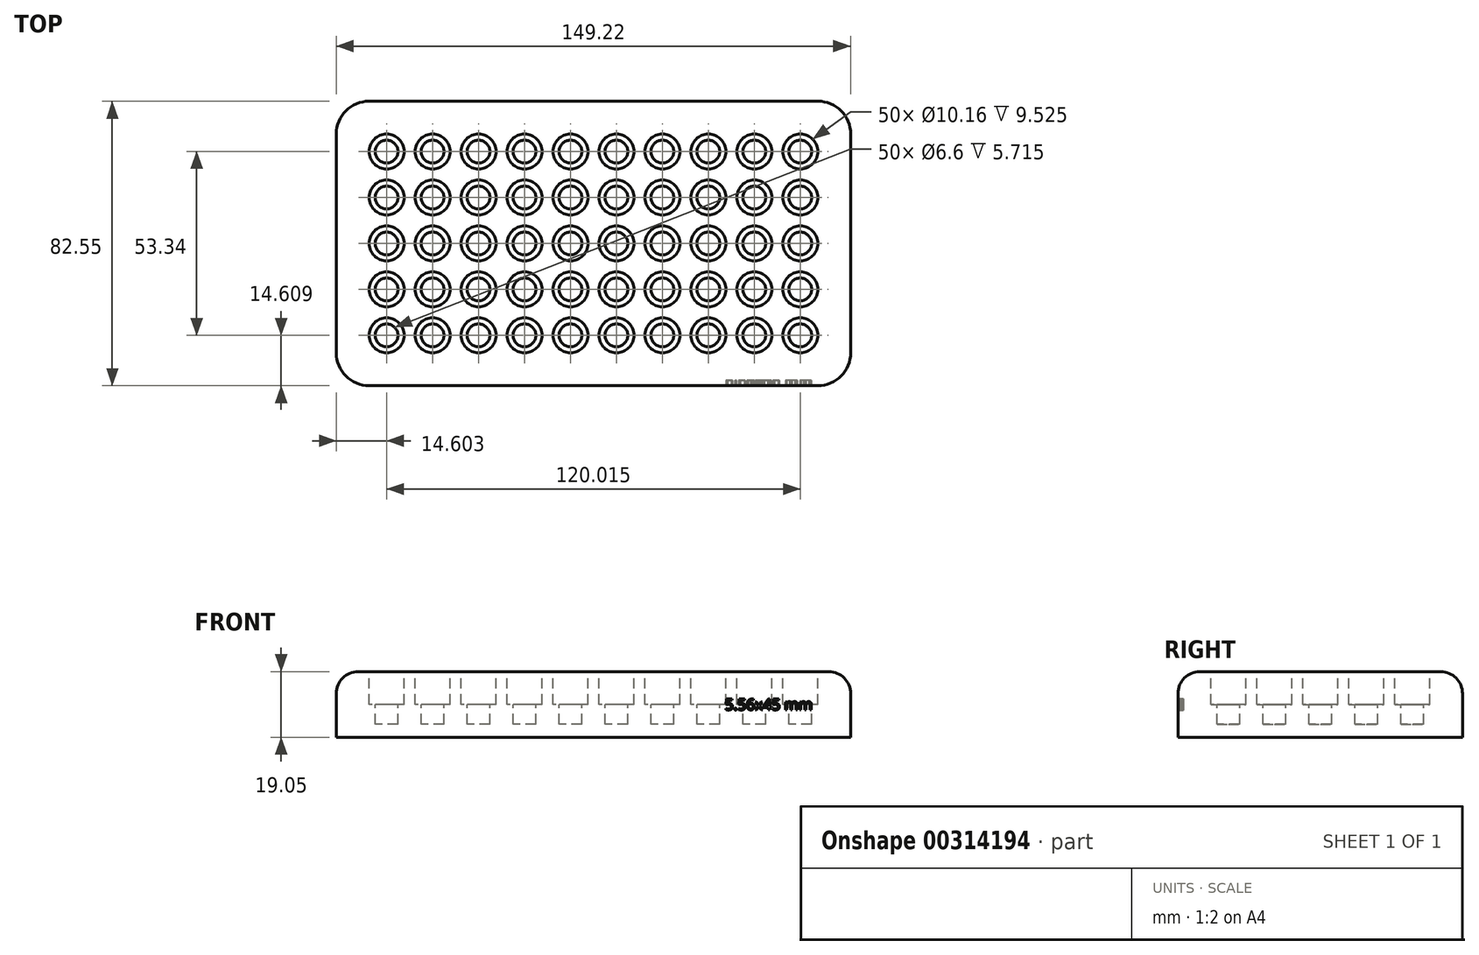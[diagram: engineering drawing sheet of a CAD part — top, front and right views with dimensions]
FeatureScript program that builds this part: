
annotation { "Feature Type Name" : "Feature", "Feature Type Description" : "" }
export const myFeature = defineFeature(function(context is Context, id is Id, definition is map)
    precondition{}
    {
        {
            var Q0;
            Q0=qCreatedBy(makeId("Top.planeOp"),FACE);
            var sketch = newSketch(context, id + "F0", { "sketchPlane" : qUnion([Q0])});
            skLineSegment(sketch, "E0.bottom", {"start": v(-34.12, 87.4) * mm, "end": v(96.06, 87.4) * mm});
            skLineSegment(sketch, "E0.top", {"start": v(-34.12, 4.85) * mm, "end": v(96.06, 4.85) * mm});
            skLineSegment(sketch, "E0.left", {"start": v(-43.64, 77.88) * mm, "end": v(-43.64, 14.38) * mm});
            skLineSegment(sketch, "E0.right", {"start": v(105.58, 77.88) * mm, "end": v(105.58, 14.38) * mm});
            skPoint(sketch, "E1.visualSharp", {"position": v(-43.64, 87.4) * mm});
            skArc(sketch, "E1.filletArc", {"start": v(-34.12, 87.4) * mm, "mid": v(-40.85, 84.61) * mm, "end": v(-43.64, 77.88) * mm});
            skPoint(sketch, "E2.visualSharp", {"position": v(-43.64, 4.85) * mm});
            skArc(sketch, "E2.filletArc", {"start": v(-43.64, 14.38) * mm, "mid": v(-40.85, 7.64) * mm, "end": v(-34.12, 4.85) * mm});
            skPoint(sketch, "E3.visualSharp", {"position": v(105.58, 4.85) * mm});
            skArc(sketch, "E3.filletArc", {"start": v(96.06, 4.85) * mm, "mid": v(102.8, 7.64) * mm, "end": v(105.58, 14.38) * mm});
            skPoint(sketch, "E4.visualSharp", {"position": v(105.58, 87.4) * mm});
            skArc(sketch, "E4.filletArc", {"start": v(105.58, 77.88) * mm, "mid": v(102.8, 84.61) * mm, "end": v(96.06, 87.4) * mm});
            skSolve(sketch);
        }
        {
            var Q0;
            Q0=makeQuery(id+"F0.imprint","IMPRINT",FACE,{"disambiguationData":[TD([[makeQuery(id+"F0.imprint","IMPRINT",EDGE,{"derivedFrom":sQuery(id+"F0.wireOp",EDGE,"E0.bottom")}),-1.0]])]});
            extrude(context, id + "F1", {"entities" : qUnion([Q0]), "depth" : 19.05 * mm});
        }
        {
            var Q0;
            Q0=makeQuery(id+"F1.opExtrude","CAP_EDGE",EDGE,{"disambiguationData":[OSD([sQuery(id+"F0.wireOp",EDGE,"E0.top")])],"isStart":false});
            fillet(context, id + "F2", {"entities" : qUnion([Q0]), "radius" : 6.35 * mm, "tangentPropagation" : true, "allowEdgeOverflow" : false});
        }
        {
            var Q0;
            Q0=makeQuery(id+"F1.opExtrude","CAP_FACE",FACE,{"disambiguationData":[OSD([sQuery(id+"F0.wireOp",EDGE,"E0.bottom"),sQuery(id+"F0.wireOp",EDGE,"E0.top"),sQuery(id+"F0.wireOp",EDGE,"E0.left"),sQuery(id+"F0.wireOp",EDGE,"E0.right"),sQuery(id+"F0.wireOp",EDGE,"E1.filletArc"),sQuery(id+"F0.wireOp",EDGE,"E2.filletArc"),sQuery(id+"F0.wireOp",EDGE,"E3.filletArc"),sQuery(id+"F0.wireOp",EDGE,"E4.filletArc")])],"isStart":false});
            var sketch = newSketch(context, id + "F3", { "sketchPlane" : qUnion([Q0])});
            skCircle(sketch, "E5", {"center": v(-29.04, 72.8) * mm, "radius": 5.08 * mm});
            skCircle(sketch, "E6.1.0.0", {"center": v(-15.7, 72.8) * mm, "radius": 5.08 * mm});
            skCircle(sketch, "E6.2.0.0", {"center": v(-2.37, 72.8) * mm, "radius": 5.08 * mm});
            skCircle(sketch, "E6.3.0.0", {"center": v(10.97, 72.8) * mm, "radius": 5.08 * mm});
            skCircle(sketch, "E6.4.0.0", {"center": v(24.3, 72.8) * mm, "radius": 5.08 * mm});
            skCircle(sketch, "E6.5.0.0", {"center": v(37.64, 72.8) * mm, "radius": 5.08 * mm});
            skCircle(sketch, "E6.6.0.0", {"center": v(50.97, 72.8) * mm, "radius": 5.08 * mm});
            skCircle(sketch, "E6.7.0.0", {"center": v(64.3, 72.8) * mm, "radius": 5.08 * mm});
            skCircle(sketch, "E6.8.0.0", {"center": v(77.64, 72.8) * mm, "radius": 5.08 * mm});
            skCircle(sketch, "E6.9.0.0", {"center": v(90.98, 72.8) * mm, "radius": 5.08 * mm});
            skLineSegment(sketch, "E6.direction1", {"start": v(-29.04, 72.8) * mm, "end": v(-15.7, 72.8) * mm, "construction": true});
            skCircle(sketch, "E7.1.0.0", {"center": v(90.98, 59.46) * mm, "radius": 5.08 * mm});
            skCircle(sketch, "E7.2.0.0", {"center": v(90.98, 46.13) * mm, "radius": 5.08 * mm});
            skCircle(sketch, "E7.3.0.0", {"center": v(90.98, 32.8) * mm, "radius": 5.08 * mm});
            skCircle(sketch, "E7.4.0.0", {"center": v(90.98, 19.46) * mm, "radius": 5.08 * mm});
            skLineSegment(sketch, "E7.direction1", {"start": v(90.98, 72.8) * mm, "end": v(90.98, 59.46) * mm, "construction": true});
            skCircle(sketch, "E8.1.0.0", {"center": v(77.64, 59.46) * mm, "radius": 5.08 * mm});
            skCircle(sketch, "E8.2.0.0", {"center": v(77.64, 46.13) * mm, "radius": 5.08 * mm});
            skCircle(sketch, "E8.3.0.0", {"center": v(77.64, 32.8) * mm, "radius": 5.08 * mm});
            skCircle(sketch, "E8.4.0.0", {"center": v(77.64, 19.46) * mm, "radius": 5.08 * mm});
            skLineSegment(sketch, "E8.direction1", {"start": v(77.64, 72.8) * mm, "end": v(77.64, 59.46) * mm, "construction": true});
            skCircle(sketch, "E9.1.0.0", {"center": v(64.3, 59.46) * mm, "radius": 5.08 * mm});
            skCircle(sketch, "E9.2.0.0", {"center": v(64.3, 46.13) * mm, "radius": 5.08 * mm});
            skCircle(sketch, "E9.3.0.0", {"center": v(64.3, 32.8) * mm, "radius": 5.08 * mm});
            skCircle(sketch, "E9.4.0.0", {"center": v(64.3, 19.46) * mm, "radius": 5.08 * mm});
            skLineSegment(sketch, "E9.direction1", {"start": v(64.3, 72.8) * mm, "end": v(64.3, 59.46) * mm, "construction": true});
            skCircle(sketch, "E10.1.0.0", {"center": v(50.97, 59.46) * mm, "radius": 5.08 * mm});
            skCircle(sketch, "E10.2.0.0", {"center": v(37.64, 59.46) * mm, "radius": 5.08 * mm});
            skCircle(sketch, "E10.3.0.0", {"center": v(24.3, 59.46) * mm, "radius": 5.08 * mm});
            skCircle(sketch, "E10.4.0.0", {"center": v(10.97, 59.46) * mm, "radius": 5.08 * mm});
            skCircle(sketch, "E10.5.0.0", {"center": v(-2.37, 59.46) * mm, "radius": 5.08 * mm});
            skCircle(sketch, "E10.6.0.0", {"center": v(-15.7, 59.46) * mm, "radius": 5.08 * mm});
            skCircle(sketch, "E10.7.0.0", {"center": v(-29.04, 59.46) * mm, "radius": 5.08 * mm});
            skLineSegment(sketch, "E10.direction1", {"start": v(64.3, 59.46) * mm, "end": v(50.97, 59.46) * mm, "construction": true});
            skCircle(sketch, "E11.1.0.0", {"center": v(50.97, 46.13) * mm, "radius": 5.08 * mm});
            skCircle(sketch, "E11.2.0.0", {"center": v(37.64, 46.13) * mm, "radius": 5.08 * mm});
            skCircle(sketch, "E11.3.0.0", {"center": v(24.3, 46.13) * mm, "radius": 5.08 * mm});
            skCircle(sketch, "E11.4.0.0", {"center": v(10.97, 46.13) * mm, "radius": 5.08 * mm});
            skCircle(sketch, "E11.5.0.0", {"center": v(-2.37, 46.13) * mm, "radius": 5.08 * mm});
            skCircle(sketch, "E11.6.0.0", {"center": v(-15.7, 46.13) * mm, "radius": 5.08 * mm});
            skCircle(sketch, "E11.7.0.0", {"center": v(-29.04, 46.13) * mm, "radius": 5.08 * mm});
            skLineSegment(sketch, "E11.direction1", {"start": v(64.3, 46.13) * mm, "end": v(50.97, 46.13) * mm, "construction": true});
            skCircle(sketch, "E12.1.0.0", {"center": v(50.97, 32.8) * mm, "radius": 5.08 * mm});
            skCircle(sketch, "E12.2.0.0", {"center": v(37.64, 32.8) * mm, "radius": 5.08 * mm});
            skCircle(sketch, "E12.3.0.0", {"center": v(24.3, 32.8) * mm, "radius": 5.08 * mm});
            skCircle(sketch, "E12.4.0.0", {"center": v(10.97, 32.8) * mm, "radius": 5.08 * mm});
            skCircle(sketch, "E12.5.0.0", {"center": v(-2.37, 32.8) * mm, "radius": 5.08 * mm});
            skCircle(sketch, "E12.6.0.0", {"center": v(-15.7, 32.8) * mm, "radius": 5.08 * mm});
            skCircle(sketch, "E12.7.0.0", {"center": v(-29.04, 32.8) * mm, "radius": 5.08 * mm});
            skLineSegment(sketch, "E12.direction1", {"start": v(64.3, 32.8) * mm, "end": v(50.97, 32.8) * mm, "construction": true});
            skCircle(sketch, "E13.1.0.0", {"center": v(50.97, 19.46) * mm, "radius": 5.08 * mm});
            skCircle(sketch, "E13.2.0.0", {"center": v(37.64, 19.46) * mm, "radius": 5.08 * mm});
            skCircle(sketch, "E13.3.0.0", {"center": v(24.3, 19.46) * mm, "radius": 5.08 * mm});
            skCircle(sketch, "E13.4.0.0", {"center": v(10.97, 19.46) * mm, "radius": 5.08 * mm});
            skCircle(sketch, "E13.5.0.0", {"center": v(-2.37, 19.46) * mm, "radius": 5.08 * mm});
            skCircle(sketch, "E13.6.0.0", {"center": v(-15.7, 19.46) * mm, "radius": 5.08 * mm});
            skCircle(sketch, "E13.7.0.0", {"center": v(-29.04, 19.46) * mm, "radius": 5.08 * mm});
            skLineSegment(sketch, "E13.direction1", {"start": v(64.3, 19.46) * mm, "end": v(50.97, 19.46) * mm, "construction": true});
            skSolve(sketch);
        }
        {
            var Q0;
            Q0=makeQuery(id+"F3.imprint","IMPRINT",FACE,{"disambiguationData":[TD([[makeQuery(id+"F3.imprint","IMPRINT",EDGE,{"derivedFrom":sQuery(id+"F3.wireOp",EDGE,"E5")}),1.0]])]});
            var Q1;
            Q1=makeQuery(id+"F3.imprint","IMPRINT",FACE,{"disambiguationData":[TD([[makeQuery(id+"F3.imprint","IMPRINT",EDGE,{"derivedFrom":sQuery(id+"F3.wireOp",EDGE,"E6.1.0.0")}),1.0]])]});
            var Q2;
            Q2=makeQuery(id+"F3.imprint","IMPRINT",FACE,{"disambiguationData":[TD([[makeQuery(id+"F3.imprint","IMPRINT",EDGE,{"derivedFrom":sQuery(id+"F3.wireOp",EDGE,"E6.2.0.0")}),1.0]])]});
            var Q3;
            Q3=makeQuery(id+"F3.imprint","IMPRINT",FACE,{"disambiguationData":[TD([[makeQuery(id+"F3.imprint","IMPRINT",EDGE,{"derivedFrom":sQuery(id+"F3.wireOp",EDGE,"E6.3.0.0")}),1.0]])]});
            var Q4;
            Q4=makeQuery(id+"F3.imprint","IMPRINT",FACE,{"disambiguationData":[TD([[makeQuery(id+"F3.imprint","IMPRINT",EDGE,{"derivedFrom":sQuery(id+"F3.wireOp",EDGE,"E6.4.0.0")}),1.0]])]});
            var Q5;
            Q5=makeQuery(id+"F3.imprint","IMPRINT",FACE,{"disambiguationData":[TD([[makeQuery(id+"F3.imprint","IMPRINT",EDGE,{"derivedFrom":sQuery(id+"F3.wireOp",EDGE,"E6.5.0.0")}),1.0]])]});
            var Q6;
            Q6=makeQuery(id+"F3.imprint","IMPRINT",FACE,{"disambiguationData":[TD([[makeQuery(id+"F3.imprint","IMPRINT",EDGE,{"derivedFrom":sQuery(id+"F3.wireOp",EDGE,"E6.7.0.0")}),1.0]])]});
            var Q7;
            Q7=makeQuery(id+"F3.imprint","IMPRINT",FACE,{"disambiguationData":[TD([[makeQuery(id+"F3.imprint","IMPRINT",EDGE,{"derivedFrom":sQuery(id+"F3.wireOp",EDGE,"E6.6.0.0")}),1.0]])]});
            var Q8;
            Q8=makeQuery(id+"F3.imprint","IMPRINT",FACE,{"disambiguationData":[TD([[makeQuery(id+"F3.imprint","IMPRINT",EDGE,{"derivedFrom":sQuery(id+"F3.wireOp",EDGE,"E6.9.0.0")}),1.0]])]});
            var Q9;
            Q9=makeQuery(id+"F3.imprint","IMPRINT",FACE,{"disambiguationData":[TD([[makeQuery(id+"F3.imprint","IMPRINT",EDGE,{"derivedFrom":sQuery(id+"F3.wireOp",EDGE,"E6.8.0.0")}),1.0]])]});
            var Q10;
            Q10=makeQuery(id+"F3.imprint","IMPRINT",FACE,{"disambiguationData":[TD([[makeQuery(id+"F3.imprint","IMPRINT",EDGE,{"derivedFrom":sQuery(id+"F3.wireOp",EDGE,"E10.7.0.0")}),1.0]])]});
            var Q11;
            Q11=makeQuery(id+"F3.imprint","IMPRINT",FACE,{"disambiguationData":[TD([[makeQuery(id+"F3.imprint","IMPRINT",EDGE,{"derivedFrom":sQuery(id+"F3.wireOp",EDGE,"E10.6.0.0")}),1.0]])]});
            var Q12;
            Q12=makeQuery(id+"F3.imprint","IMPRINT",FACE,{"disambiguationData":[TD([[makeQuery(id+"F3.imprint","IMPRINT",EDGE,{"derivedFrom":sQuery(id+"F3.wireOp",EDGE,"E10.5.0.0")}),1.0]])]});
            var Q13;
            Q13=makeQuery(id+"F3.imprint","IMPRINT",FACE,{"disambiguationData":[TD([[makeQuery(id+"F3.imprint","IMPRINT",EDGE,{"derivedFrom":sQuery(id+"F3.wireOp",EDGE,"E10.4.0.0")}),1.0]])]});
            var Q14;
            Q14=makeQuery(id+"F3.imprint","IMPRINT",FACE,{"disambiguationData":[TD([[makeQuery(id+"F3.imprint","IMPRINT",EDGE,{"derivedFrom":sQuery(id+"F3.wireOp",EDGE,"E10.3.0.0")}),1.0]])]});
            var Q15;
            Q15=makeQuery(id+"F3.imprint","IMPRINT",FACE,{"disambiguationData":[TD([[makeQuery(id+"F3.imprint","IMPRINT",EDGE,{"derivedFrom":sQuery(id+"F3.wireOp",EDGE,"E10.2.0.0")}),1.0]])]});
            var Q16;
            Q16=makeQuery(id+"F3.imprint","IMPRINT",FACE,{"disambiguationData":[TD([[makeQuery(id+"F3.imprint","IMPRINT",EDGE,{"derivedFrom":sQuery(id+"F3.wireOp",EDGE,"E10.1.0.0")}),1.0]])]});
            var Q17;
            Q17=makeQuery(id+"F3.imprint","IMPRINT",FACE,{"disambiguationData":[TD([[makeQuery(id+"F3.imprint","IMPRINT",EDGE,{"derivedFrom":sQuery(id+"F3.wireOp",EDGE,"E9.1.0.0")}),1.0]])]});
            var Q18;
            Q18=makeQuery(id+"F3.imprint","IMPRINT",FACE,{"disambiguationData":[TD([[makeQuery(id+"F3.imprint","IMPRINT",EDGE,{"derivedFrom":sQuery(id+"F3.wireOp",EDGE,"E8.1.0.0")}),1.0]])]});
            var Q19;
            Q19=makeQuery(id+"F3.imprint","IMPRINT",FACE,{"disambiguationData":[TD([[makeQuery(id+"F3.imprint","IMPRINT",EDGE,{"derivedFrom":sQuery(id+"F3.wireOp",EDGE,"E7.1.0.0")}),1.0]])]});
            var Q20;
            Q20=makeQuery(id+"F3.imprint","IMPRINT",FACE,{"disambiguationData":[TD([[makeQuery(id+"F3.imprint","IMPRINT",EDGE,{"derivedFrom":sQuery(id+"F3.wireOp",EDGE,"E7.2.0.0")}),1.0]])]});
            var Q21;
            Q21=makeQuery(id+"F3.imprint","IMPRINT",FACE,{"disambiguationData":[TD([[makeQuery(id+"F3.imprint","IMPRINT",EDGE,{"derivedFrom":sQuery(id+"F3.wireOp",EDGE,"E8.2.0.0")}),1.0]])]});
            var Q22;
            Q22=makeQuery(id+"F3.imprint","IMPRINT",FACE,{"disambiguationData":[TD([[makeQuery(id+"F3.imprint","IMPRINT",EDGE,{"derivedFrom":sQuery(id+"F3.wireOp",EDGE,"E9.2.0.0")}),1.0]])]});
            var Q23;
            Q23=makeQuery(id+"F3.imprint","IMPRINT",FACE,{"disambiguationData":[TD([[makeQuery(id+"F3.imprint","IMPRINT",EDGE,{"derivedFrom":sQuery(id+"F3.wireOp",EDGE,"E11.1.0.0")}),1.0]])]});
            var Q24;
            Q24=makeQuery(id+"F3.imprint","IMPRINT",FACE,{"disambiguationData":[TD([[makeQuery(id+"F3.imprint","IMPRINT",EDGE,{"derivedFrom":sQuery(id+"F3.wireOp",EDGE,"E11.2.0.0")}),1.0]])]});
            var Q25;
            Q25=makeQuery(id+"F3.imprint","IMPRINT",FACE,{"disambiguationData":[TD([[makeQuery(id+"F3.imprint","IMPRINT",EDGE,{"derivedFrom":sQuery(id+"F3.wireOp",EDGE,"E11.3.0.0")}),1.0]])]});
            var Q26;
            Q26=makeQuery(id+"F3.imprint","IMPRINT",FACE,{"disambiguationData":[TD([[makeQuery(id+"F3.imprint","IMPRINT",EDGE,{"derivedFrom":sQuery(id+"F3.wireOp",EDGE,"E11.4.0.0")}),1.0]])]});
            var Q27;
            Q27=makeQuery(id+"F3.imprint","IMPRINT",FACE,{"disambiguationData":[TD([[makeQuery(id+"F3.imprint","IMPRINT",EDGE,{"derivedFrom":sQuery(id+"F3.wireOp",EDGE,"E11.5.0.0")}),1.0]])]});
            var Q28;
            Q28=makeQuery(id+"F3.imprint","IMPRINT",FACE,{"disambiguationData":[TD([[makeQuery(id+"F3.imprint","IMPRINT",EDGE,{"derivedFrom":sQuery(id+"F3.wireOp",EDGE,"E11.6.0.0")}),1.0]])]});
            var Q29;
            Q29=makeQuery(id+"F3.imprint","IMPRINT",FACE,{"disambiguationData":[TD([[makeQuery(id+"F3.imprint","IMPRINT",EDGE,{"derivedFrom":sQuery(id+"F3.wireOp",EDGE,"E11.7.0.0")}),1.0]])]});
            var Q30;
            Q30=makeQuery(id+"F3.imprint","IMPRINT",FACE,{"disambiguationData":[TD([[makeQuery(id+"F3.imprint","IMPRINT",EDGE,{"derivedFrom":sQuery(id+"F3.wireOp",EDGE,"E12.7.0.0")}),1.0]])]});
            var Q31;
            Q31=makeQuery(id+"F3.imprint","IMPRINT",FACE,{"disambiguationData":[TD([[makeQuery(id+"F3.imprint","IMPRINT",EDGE,{"derivedFrom":sQuery(id+"F3.wireOp",EDGE,"E12.6.0.0")}),1.0]])]});
            var Q32;
            Q32=makeQuery(id+"F3.imprint","IMPRINT",FACE,{"disambiguationData":[TD([[makeQuery(id+"F3.imprint","IMPRINT",EDGE,{"derivedFrom":sQuery(id+"F3.wireOp",EDGE,"E12.5.0.0")}),1.0]])]});
            var Q33;
            Q33=makeQuery(id+"F3.imprint","IMPRINT",FACE,{"disambiguationData":[TD([[makeQuery(id+"F3.imprint","IMPRINT",EDGE,{"derivedFrom":sQuery(id+"F3.wireOp",EDGE,"E12.4.0.0")}),1.0]])]});
            var Q34;
            Q34=makeQuery(id+"F3.imprint","IMPRINT",FACE,{"disambiguationData":[TD([[makeQuery(id+"F3.imprint","IMPRINT",EDGE,{"derivedFrom":sQuery(id+"F3.wireOp",EDGE,"E12.3.0.0")}),1.0]])]});
            var Q35;
            Q35=makeQuery(id+"F3.imprint","IMPRINT",FACE,{"disambiguationData":[TD([[makeQuery(id+"F3.imprint","IMPRINT",EDGE,{"derivedFrom":sQuery(id+"F3.wireOp",EDGE,"E12.2.0.0")}),1.0]])]});
            var Q36;
            Q36=makeQuery(id+"F3.imprint","IMPRINT",FACE,{"disambiguationData":[TD([[makeQuery(id+"F3.imprint","IMPRINT",EDGE,{"derivedFrom":sQuery(id+"F3.wireOp",EDGE,"E12.1.0.0")}),1.0]])]});
            var Q37;
            Q37=makeQuery(id+"F3.imprint","IMPRINT",FACE,{"disambiguationData":[TD([[makeQuery(id+"F3.imprint","IMPRINT",EDGE,{"derivedFrom":sQuery(id+"F3.wireOp",EDGE,"E9.3.0.0")}),1.0]])]});
            var Q38;
            Q38=makeQuery(id+"F3.imprint","IMPRINT",FACE,{"disambiguationData":[TD([[makeQuery(id+"F3.imprint","IMPRINT",EDGE,{"derivedFrom":sQuery(id+"F3.wireOp",EDGE,"E8.3.0.0")}),1.0]])]});
            var Q39;
            Q39=makeQuery(id+"F3.imprint","IMPRINT",FACE,{"disambiguationData":[TD([[makeQuery(id+"F3.imprint","IMPRINT",EDGE,{"derivedFrom":sQuery(id+"F3.wireOp",EDGE,"E7.3.0.0")}),1.0]])]});
            var Q40;
            Q40=makeQuery(id+"F3.imprint","IMPRINT",FACE,{"disambiguationData":[TD([[makeQuery(id+"F3.imprint","IMPRINT",EDGE,{"derivedFrom":sQuery(id+"F3.wireOp",EDGE,"E7.4.0.0")}),1.0]])]});
            var Q41;
            Q41=makeQuery(id+"F3.imprint","IMPRINT",FACE,{"disambiguationData":[TD([[makeQuery(id+"F3.imprint","IMPRINT",EDGE,{"derivedFrom":sQuery(id+"F3.wireOp",EDGE,"E8.4.0.0")}),1.0]])]});
            var Q42;
            Q42=makeQuery(id+"F3.imprint","IMPRINT",FACE,{"disambiguationData":[TD([[makeQuery(id+"F3.imprint","IMPRINT",EDGE,{"derivedFrom":sQuery(id+"F3.wireOp",EDGE,"E9.4.0.0")}),1.0]])]});
            var Q43;
            Q43=makeQuery(id+"F3.imprint","IMPRINT",FACE,{"disambiguationData":[TD([[makeQuery(id+"F3.imprint","IMPRINT",EDGE,{"derivedFrom":sQuery(id+"F3.wireOp",EDGE,"E13.1.0.0")}),1.0]])]});
            var Q44;
            Q44=makeQuery(id+"F3.imprint","IMPRINT",FACE,{"disambiguationData":[TD([[makeQuery(id+"F3.imprint","IMPRINT",EDGE,{"derivedFrom":sQuery(id+"F3.wireOp",EDGE,"E13.2.0.0")}),1.0]])]});
            var Q45;
            Q45=makeQuery(id+"F3.imprint","IMPRINT",FACE,{"disambiguationData":[TD([[makeQuery(id+"F3.imprint","IMPRINT",EDGE,{"derivedFrom":sQuery(id+"F3.wireOp",EDGE,"E13.3.0.0")}),1.0]])]});
            var Q46;
            Q46=makeQuery(id+"F3.imprint","IMPRINT",FACE,{"disambiguationData":[TD([[makeQuery(id+"F3.imprint","IMPRINT",EDGE,{"derivedFrom":sQuery(id+"F3.wireOp",EDGE,"E13.4.0.0")}),1.0]])]});
            var Q47;
            Q47=makeQuery(id+"F3.imprint","IMPRINT",FACE,{"disambiguationData":[TD([[makeQuery(id+"F3.imprint","IMPRINT",EDGE,{"derivedFrom":sQuery(id+"F3.wireOp",EDGE,"E13.5.0.0")}),1.0]])]});
            var Q48;
            Q48=makeQuery(id+"F3.imprint","IMPRINT",FACE,{"disambiguationData":[TD([[makeQuery(id+"F3.imprint","IMPRINT",EDGE,{"derivedFrom":sQuery(id+"F3.wireOp",EDGE,"E13.6.0.0")}),1.0]])]});
            var Q49;
            Q49=makeQuery(id+"F3.imprint","IMPRINT",FACE,{"disambiguationData":[TD([[makeQuery(id+"F3.imprint","IMPRINT",EDGE,{"derivedFrom":sQuery(id+"F3.wireOp",EDGE,"E13.7.0.0")}),1.0]])]});
            extrude(context, id + "F4", {"entities" : qUnion([Q0, Q1, Q2, Q3, Q4, Q5, Q6, Q7, Q8, Q9, Q10, Q11, Q12, Q13, Q14, Q15, Q16, Q17, Q18, Q19, Q20, Q21, Q22, Q23, Q24, Q25, Q26, Q27, Q28, Q29, Q30, Q31, Q32, Q33, Q34, Q35, Q36, Q37, Q38, Q39, Q40, Q41, Q42, Q43, Q44, Q45, Q46, Q47, Q48, Q49]), "operationType" : NewBodyOperationType.REMOVE, "oppositeDirection" : true, "depth" : 9.52 * mm});
        }
        {
            var Q0;
            Q0=makeQuery(id+"F1.opExtrude","CAP_FACE",FACE,{"disambiguationData":[OSD([sQuery(id+"F0.wireOp",EDGE,"E0.bottom"),sQuery(id+"F0.wireOp",EDGE,"E0.top"),sQuery(id+"F0.wireOp",EDGE,"E0.left"),sQuery(id+"F0.wireOp",EDGE,"E0.right"),sQuery(id+"F0.wireOp",EDGE,"E1.filletArc"),sQuery(id+"F0.wireOp",EDGE,"E2.filletArc"),sQuery(id+"F0.wireOp",EDGE,"E3.filletArc"),sQuery(id+"F0.wireOp",EDGE,"E4.filletArc")])],"isStart":false});
            var sketch = newSketch(context, id + "F5", { "sketchPlane" : qUnion([Q0])});
            skCircle(sketch, "E14", {"center": v(-29.04, 72.8) * mm, "radius": 3.3 * mm});
            skCircle(sketch, "E15.1.0.0", {"center": v(-29.04, 59.46) * mm, "radius": 3.3 * mm});
            skCircle(sketch, "E15.2.0.0", {"center": v(-29.04, 46.13) * mm, "radius": 3.3 * mm});
            skCircle(sketch, "E15.3.0.0", {"center": v(-29.04, 32.8) * mm, "radius": 3.3 * mm});
            skCircle(sketch, "E15.4.0.0", {"center": v(-29.04, 19.46) * mm, "radius": 3.3 * mm});
            skLineSegment(sketch, "E15.direction1", {"start": v(-29.04, 72.8) * mm, "end": v(-29.04, 59.46) * mm, "construction": true});
            skCircle(sketch, "E16.1.0.0", {"center": v(-15.7, 72.8) * mm, "radius": 3.3 * mm});
            skCircle(sketch, "E16.2.0.0", {"center": v(-2.37, 72.8) * mm, "radius": 3.3 * mm});
            skCircle(sketch, "E16.3.0.0", {"center": v(10.97, 72.8) * mm, "radius": 3.3 * mm});
            skCircle(sketch, "E16.4.0.0", {"center": v(24.3, 72.8) * mm, "radius": 3.3 * mm});
            skCircle(sketch, "E16.5.0.0", {"center": v(37.64, 72.8) * mm, "radius": 3.3 * mm});
            skCircle(sketch, "E16.6.0.0", {"center": v(50.97, 72.8) * mm, "radius": 3.3 * mm});
            skCircle(sketch, "E16.7.0.0", {"center": v(64.3, 72.8) * mm, "radius": 3.3 * mm});
            skCircle(sketch, "E16.8.0.0", {"center": v(77.64, 72.8) * mm, "radius": 3.3 * mm});
            skCircle(sketch, "E16.9.0.0", {"center": v(90.98, 72.8) * mm, "radius": 3.3 * mm});
            skLineSegment(sketch, "E16.direction1", {"start": v(-29.04, 72.8) * mm, "end": v(-15.7, 72.8) * mm, "construction": true});
            skCircle(sketch, "E17.1.0.0", {"center": v(-15.7, 59.46) * mm, "radius": 3.3 * mm});
            skCircle(sketch, "E17.2.0.0", {"center": v(-2.37, 59.46) * mm, "radius": 3.3 * mm});
            skCircle(sketch, "E17.3.0.0", {"center": v(10.97, 59.46) * mm, "radius": 3.3 * mm});
            skCircle(sketch, "E17.4.0.0", {"center": v(24.3, 59.46) * mm, "radius": 3.3 * mm});
            skCircle(sketch, "E17.5.0.0", {"center": v(37.64, 59.46) * mm, "radius": 3.3 * mm});
            skCircle(sketch, "E17.6.0.0", {"center": v(50.97, 59.46) * mm, "radius": 3.3 * mm});
            skCircle(sketch, "E17.7.0.0", {"center": v(64.3, 59.46) * mm, "radius": 3.3 * mm});
            skCircle(sketch, "E17.8.0.0", {"center": v(77.64, 59.46) * mm, "radius": 3.3 * mm});
            skCircle(sketch, "E17.9.0.0", {"center": v(90.98, 59.46) * mm, "radius": 3.3 * mm});
            skLineSegment(sketch, "E17.direction1", {"start": v(-29.04, 59.46) * mm, "end": v(-15.7, 59.46) * mm, "construction": true});
            skCircle(sketch, "E18.1.0.0", {"center": v(-15.7, 46.13) * mm, "radius": 3.3 * mm});
            skCircle(sketch, "E18.2.0.0", {"center": v(-2.37, 46.13) * mm, "radius": 3.3 * mm});
            skCircle(sketch, "E18.3.0.0", {"center": v(10.97, 46.13) * mm, "radius": 3.3 * mm});
            skCircle(sketch, "E18.4.0.0", {"center": v(24.3, 46.13) * mm, "radius": 3.3 * mm});
            skCircle(sketch, "E18.5.0.0", {"center": v(37.64, 46.13) * mm, "radius": 3.3 * mm});
            skCircle(sketch, "E18.6.0.0", {"center": v(50.97, 46.13) * mm, "radius": 3.3 * mm});
            skCircle(sketch, "E18.7.0.0", {"center": v(64.3, 46.13) * mm, "radius": 3.3 * mm});
            skCircle(sketch, "E18.8.0.0", {"center": v(77.64, 46.13) * mm, "radius": 3.3 * mm});
            skCircle(sketch, "E18.9.0.0", {"center": v(90.98, 46.13) * mm, "radius": 3.3 * mm});
            skLineSegment(sketch, "E18.direction1", {"start": v(-29.04, 46.13) * mm, "end": v(-15.7, 46.13) * mm, "construction": true});
            skCircle(sketch, "E19.1.0.0", {"center": v(-15.7, 32.8) * mm, "radius": 3.3 * mm});
            skCircle(sketch, "E19.2.0.0", {"center": v(-2.37, 32.8) * mm, "radius": 3.3 * mm});
            skCircle(sketch, "E19.3.0.0", {"center": v(10.97, 32.8) * mm, "radius": 3.3 * mm});
            skCircle(sketch, "E19.4.0.0", {"center": v(24.3, 32.8) * mm, "radius": 3.3 * mm});
            skCircle(sketch, "E19.5.0.0", {"center": v(37.64, 32.8) * mm, "radius": 3.3 * mm});
            skCircle(sketch, "E19.6.0.0", {"center": v(50.97, 32.8) * mm, "radius": 3.3 * mm});
            skCircle(sketch, "E19.7.0.0", {"center": v(64.3, 32.8) * mm, "radius": 3.3 * mm});
            skCircle(sketch, "E19.8.0.0", {"center": v(77.64, 32.8) * mm, "radius": 3.3 * mm});
            skCircle(sketch, "E19.9.0.0", {"center": v(90.98, 32.8) * mm, "radius": 3.3 * mm});
            skLineSegment(sketch, "E19.direction1", {"start": v(-29.04, 32.8) * mm, "end": v(-15.7, 32.8) * mm, "construction": true});
            skCircle(sketch, "E20.1.0.0", {"center": v(-15.7, 19.46) * mm, "radius": 3.3 * mm});
            skCircle(sketch, "E20.2.0.0", {"center": v(-2.37, 19.46) * mm, "radius": 3.3 * mm});
            skCircle(sketch, "E20.3.0.0", {"center": v(10.97, 19.46) * mm, "radius": 3.3 * mm});
            skCircle(sketch, "E20.4.0.0", {"center": v(24.3, 19.46) * mm, "radius": 3.3 * mm});
            skCircle(sketch, "E20.5.0.0", {"center": v(37.64, 19.46) * mm, "radius": 3.3 * mm});
            skCircle(sketch, "E20.6.0.0", {"center": v(50.97, 19.46) * mm, "radius": 3.3 * mm});
            skCircle(sketch, "E20.7.0.0", {"center": v(64.3, 19.46) * mm, "radius": 3.3 * mm});
            skCircle(sketch, "E20.8.0.0", {"center": v(77.64, 19.46) * mm, "radius": 3.3 * mm});
            skCircle(sketch, "E20.9.0.0", {"center": v(90.98, 19.46) * mm, "radius": 3.3 * mm});
            skLineSegment(sketch, "E20.direction1", {"start": v(-29.04, 19.46) * mm, "end": v(-15.7, 19.46) * mm, "construction": true});
            skSolve(sketch);
        }
        {
            var Q0;
            Q0=makeQuery(id+"F5.imprint","IMPRINT",FACE,{"disambiguationData":[TD([[makeQuery(id+"F5.imprint","IMPRINT",EDGE,{"derivedFrom":sQuery(id+"F5.wireOp",EDGE,"E14")}),1.0]])]});
            var Q1;
            Q1=makeQuery(id+"F5.imprint","IMPRINT",FACE,{"disambiguationData":[TD([[makeQuery(id+"F5.imprint","IMPRINT",EDGE,{"derivedFrom":sQuery(id+"F5.wireOp",EDGE,"E16.1.0.0")}),1.0]])]});
            var Q2;
            Q2=makeQuery(id+"F5.imprint","IMPRINT",FACE,{"disambiguationData":[TD([[makeQuery(id+"F5.imprint","IMPRINT",EDGE,{"derivedFrom":sQuery(id+"F5.wireOp",EDGE,"E16.2.0.0")}),1.0]])]});
            var Q3;
            Q3=makeQuery(id+"F5.imprint","IMPRINT",FACE,{"disambiguationData":[TD([[makeQuery(id+"F5.imprint","IMPRINT",EDGE,{"derivedFrom":sQuery(id+"F5.wireOp",EDGE,"E16.3.0.0")}),1.0]])]});
            var Q4;
            Q4=makeQuery(id+"F5.imprint","IMPRINT",FACE,{"disambiguationData":[TD([[makeQuery(id+"F5.imprint","IMPRINT",EDGE,{"derivedFrom":sQuery(id+"F5.wireOp",EDGE,"E16.4.0.0")}),1.0]])]});
            var Q5;
            Q5=makeQuery(id+"F5.imprint","IMPRINT",FACE,{"disambiguationData":[TD([[makeQuery(id+"F5.imprint","IMPRINT",EDGE,{"derivedFrom":sQuery(id+"F5.wireOp",EDGE,"E16.5.0.0")}),1.0]])]});
            var Q6;
            Q6=makeQuery(id+"F5.imprint","IMPRINT",FACE,{"disambiguationData":[TD([[makeQuery(id+"F5.imprint","IMPRINT",EDGE,{"derivedFrom":sQuery(id+"F5.wireOp",EDGE,"E16.6.0.0")}),1.0]])]});
            var Q7;
            Q7=makeQuery(id+"F5.imprint","IMPRINT",FACE,{"disambiguationData":[TD([[makeQuery(id+"F5.imprint","IMPRINT",EDGE,{"derivedFrom":sQuery(id+"F5.wireOp",EDGE,"E16.7.0.0")}),1.0]])]});
            var Q8;
            Q8=makeQuery(id+"F5.imprint","IMPRINT",FACE,{"disambiguationData":[TD([[makeQuery(id+"F5.imprint","IMPRINT",EDGE,{"derivedFrom":sQuery(id+"F5.wireOp",EDGE,"E16.8.0.0")}),1.0]])]});
            var Q9;
            Q9=makeQuery(id+"F5.imprint","IMPRINT",FACE,{"disambiguationData":[TD([[makeQuery(id+"F5.imprint","IMPRINT",EDGE,{"derivedFrom":sQuery(id+"F5.wireOp",EDGE,"E16.9.0.0")}),1.0]])]});
            var Q10;
            Q10=makeQuery(id+"F5.imprint","IMPRINT",FACE,{"disambiguationData":[TD([[makeQuery(id+"F5.imprint","IMPRINT",EDGE,{"derivedFrom":sQuery(id+"F5.wireOp",EDGE,"E17.9.0.0")}),1.0]])]});
            var Q11;
            Q11=makeQuery(id+"F5.imprint","IMPRINT",FACE,{"disambiguationData":[TD([[makeQuery(id+"F5.imprint","IMPRINT",EDGE,{"derivedFrom":sQuery(id+"F5.wireOp",EDGE,"E17.8.0.0")}),1.0]])]});
            var Q12;
            Q12=makeQuery(id+"F5.imprint","IMPRINT",FACE,{"disambiguationData":[TD([[makeQuery(id+"F5.imprint","IMPRINT",EDGE,{"derivedFrom":sQuery(id+"F5.wireOp",EDGE,"E17.7.0.0")}),1.0]])]});
            var Q13;
            Q13=makeQuery(id+"F5.imprint","IMPRINT",FACE,{"disambiguationData":[TD([[makeQuery(id+"F5.imprint","IMPRINT",EDGE,{"derivedFrom":sQuery(id+"F5.wireOp",EDGE,"E17.6.0.0")}),1.0]])]});
            var Q14;
            Q14=makeQuery(id+"F5.imprint","IMPRINT",FACE,{"disambiguationData":[TD([[makeQuery(id+"F5.imprint","IMPRINT",EDGE,{"derivedFrom":sQuery(id+"F5.wireOp",EDGE,"E17.4.0.0")}),1.0]])]});
            var Q15;
            Q15=makeQuery(id+"F5.imprint","IMPRINT",FACE,{"disambiguationData":[TD([[makeQuery(id+"F5.imprint","IMPRINT",EDGE,{"derivedFrom":sQuery(id+"F5.wireOp",EDGE,"E17.3.0.0")}),1.0]])]});
            var Q16;
            Q16=makeQuery(id+"F5.imprint","IMPRINT",FACE,{"disambiguationData":[TD([[makeQuery(id+"F5.imprint","IMPRINT",EDGE,{"derivedFrom":sQuery(id+"F5.wireOp",EDGE,"E17.2.0.0")}),1.0]])]});
            var Q17;
            Q17=makeQuery(id+"F5.imprint","IMPRINT",FACE,{"disambiguationData":[TD([[makeQuery(id+"F5.imprint","IMPRINT",EDGE,{"derivedFrom":sQuery(id+"F5.wireOp",EDGE,"E17.1.0.0")}),1.0]])]});
            var Q18;
            Q18=makeQuery(id+"F5.imprint","IMPRINT",FACE,{"disambiguationData":[TD([[makeQuery(id+"F5.imprint","IMPRINT",EDGE,{"derivedFrom":sQuery(id+"F5.wireOp",EDGE,"E15.1.0.0")}),1.0]])]});
            var Q19;
            Q19=makeQuery(id+"F5.imprint","IMPRINT",FACE,{"disambiguationData":[TD([[makeQuery(id+"F5.imprint","IMPRINT",EDGE,{"derivedFrom":sQuery(id+"F5.wireOp",EDGE,"E15.2.0.0")}),1.0]])]});
            var Q20;
            Q20=makeQuery(id+"F5.imprint","IMPRINT",FACE,{"disambiguationData":[TD([[makeQuery(id+"F5.imprint","IMPRINT",EDGE,{"derivedFrom":sQuery(id+"F5.wireOp",EDGE,"E18.1.0.0")}),1.0]])]});
            var Q21;
            Q21=makeQuery(id+"F5.imprint","IMPRINT",FACE,{"disambiguationData":[TD([[makeQuery(id+"F5.imprint","IMPRINT",EDGE,{"derivedFrom":sQuery(id+"F5.wireOp",EDGE,"E18.2.0.0")}),1.0]])]});
            var Q22;
            Q22=makeQuery(id+"F5.imprint","IMPRINT",FACE,{"disambiguationData":[TD([[makeQuery(id+"F5.imprint","IMPRINT",EDGE,{"derivedFrom":sQuery(id+"F5.wireOp",EDGE,"E18.3.0.0")}),1.0]])]});
            var Q23;
            Q23=makeQuery(id+"F5.imprint","IMPRINT",FACE,{"disambiguationData":[TD([[makeQuery(id+"F5.imprint","IMPRINT",EDGE,{"derivedFrom":sQuery(id+"F5.wireOp",EDGE,"E18.4.0.0")}),1.0]])]});
            var Q24;
            Q24=makeQuery(id+"F5.imprint","IMPRINT",FACE,{"disambiguationData":[TD([[makeQuery(id+"F5.imprint","IMPRINT",EDGE,{"derivedFrom":sQuery(id+"F5.wireOp",EDGE,"E18.5.0.0")}),1.0]])]});
            var Q25;
            Q25=makeQuery(id+"F5.imprint","IMPRINT",FACE,{"disambiguationData":[TD([[makeQuery(id+"F5.imprint","IMPRINT",EDGE,{"derivedFrom":sQuery(id+"F5.wireOp",EDGE,"E18.6.0.0")}),1.0]])]});
            var Q26;
            Q26=makeQuery(id+"F5.imprint","IMPRINT",FACE,{"disambiguationData":[TD([[makeQuery(id+"F5.imprint","IMPRINT",EDGE,{"derivedFrom":sQuery(id+"F5.wireOp",EDGE,"E18.7.0.0")}),1.0]])]});
            var Q27;
            Q27=makeQuery(id+"F5.imprint","IMPRINT",FACE,{"disambiguationData":[TD([[makeQuery(id+"F5.imprint","IMPRINT",EDGE,{"derivedFrom":sQuery(id+"F5.wireOp",EDGE,"E18.8.0.0")}),1.0]])]});
            var Q28;
            Q28=makeQuery(id+"F5.imprint","IMPRINT",FACE,{"disambiguationData":[TD([[makeQuery(id+"F5.imprint","IMPRINT",EDGE,{"derivedFrom":sQuery(id+"F5.wireOp",EDGE,"E18.9.0.0")}),1.0]])]});
            var Q29;
            Q29=makeQuery(id+"F5.imprint","IMPRINT",FACE,{"disambiguationData":[TD([[makeQuery(id+"F5.imprint","IMPRINT",EDGE,{"derivedFrom":sQuery(id+"F5.wireOp",EDGE,"E17.5.0.0")}),1.0]])]});
            var Q30;
            Q30=makeQuery(id+"F5.imprint","IMPRINT",FACE,{"disambiguationData":[TD([[makeQuery(id+"F5.imprint","IMPRINT",EDGE,{"derivedFrom":sQuery(id+"F5.wireOp",EDGE,"E19.9.0.0")}),1.0]])]});
            var Q31;
            Q31=makeQuery(id+"F5.imprint","IMPRINT",FACE,{"disambiguationData":[TD([[makeQuery(id+"F5.imprint","IMPRINT",EDGE,{"derivedFrom":sQuery(id+"F5.wireOp",EDGE,"E19.8.0.0")}),1.0]])]});
            var Q32;
            Q32=makeQuery(id+"F5.imprint","IMPRINT",FACE,{"disambiguationData":[TD([[makeQuery(id+"F5.imprint","IMPRINT",EDGE,{"derivedFrom":sQuery(id+"F5.wireOp",EDGE,"E19.7.0.0")}),1.0]])]});
            var Q33;
            Q33=makeQuery(id+"F5.imprint","IMPRINT",FACE,{"disambiguationData":[TD([[makeQuery(id+"F5.imprint","IMPRINT",EDGE,{"derivedFrom":sQuery(id+"F5.wireOp",EDGE,"E19.6.0.0")}),1.0]])]});
            var Q34;
            Q34=makeQuery(id+"F5.imprint","IMPRINT",FACE,{"disambiguationData":[TD([[makeQuery(id+"F5.imprint","IMPRINT",EDGE,{"derivedFrom":sQuery(id+"F5.wireOp",EDGE,"E19.5.0.0")}),1.0]])]});
            var Q35;
            Q35=makeQuery(id+"F5.imprint","IMPRINT",FACE,{"disambiguationData":[TD([[makeQuery(id+"F5.imprint","IMPRINT",EDGE,{"derivedFrom":sQuery(id+"F5.wireOp",EDGE,"E19.4.0.0")}),1.0]])]});
            var Q36;
            Q36=makeQuery(id+"F5.imprint","IMPRINT",FACE,{"disambiguationData":[TD([[makeQuery(id+"F5.imprint","IMPRINT",EDGE,{"derivedFrom":sQuery(id+"F5.wireOp",EDGE,"E19.3.0.0")}),1.0]])]});
            var Q37;
            Q37=makeQuery(id+"F5.imprint","IMPRINT",FACE,{"disambiguationData":[TD([[makeQuery(id+"F5.imprint","IMPRINT",EDGE,{"derivedFrom":sQuery(id+"F5.wireOp",EDGE,"E19.2.0.0")}),1.0]])]});
            var Q38;
            Q38=makeQuery(id+"F5.imprint","IMPRINT",FACE,{"disambiguationData":[TD([[makeQuery(id+"F5.imprint","IMPRINT",EDGE,{"derivedFrom":sQuery(id+"F5.wireOp",EDGE,"E19.1.0.0")}),1.0]])]});
            var Q39;
            Q39=makeQuery(id+"F5.imprint","IMPRINT",FACE,{"disambiguationData":[TD([[makeQuery(id+"F5.imprint","IMPRINT",EDGE,{"derivedFrom":sQuery(id+"F5.wireOp",EDGE,"E15.3.0.0")}),1.0]])]});
            var Q40;
            Q40=makeQuery(id+"F5.imprint","IMPRINT",FACE,{"disambiguationData":[TD([[makeQuery(id+"F5.imprint","IMPRINT",EDGE,{"derivedFrom":sQuery(id+"F5.wireOp",EDGE,"E15.4.0.0")}),1.0]])]});
            var Q41;
            Q41=makeQuery(id+"F5.imprint","IMPRINT",FACE,{"disambiguationData":[TD([[makeQuery(id+"F5.imprint","IMPRINT",EDGE,{"derivedFrom":sQuery(id+"F5.wireOp",EDGE,"E20.1.0.0")}),1.0]])]});
            var Q42;
            Q42=makeQuery(id+"F5.imprint","IMPRINT",FACE,{"disambiguationData":[TD([[makeQuery(id+"F5.imprint","IMPRINT",EDGE,{"derivedFrom":sQuery(id+"F5.wireOp",EDGE,"E20.2.0.0")}),1.0]])]});
            var Q43;
            Q43=makeQuery(id+"F5.imprint","IMPRINT",FACE,{"disambiguationData":[TD([[makeQuery(id+"F5.imprint","IMPRINT",EDGE,{"derivedFrom":sQuery(id+"F5.wireOp",EDGE,"E20.3.0.0")}),1.0]])]});
            var Q44;
            Q44=makeQuery(id+"F5.imprint","IMPRINT",FACE,{"disambiguationData":[TD([[makeQuery(id+"F5.imprint","IMPRINT",EDGE,{"derivedFrom":sQuery(id+"F5.wireOp",EDGE,"E20.4.0.0")}),1.0]])]});
            var Q45;
            Q45=makeQuery(id+"F5.imprint","IMPRINT",FACE,{"disambiguationData":[TD([[makeQuery(id+"F5.imprint","IMPRINT",EDGE,{"derivedFrom":sQuery(id+"F5.wireOp",EDGE,"E20.5.0.0")}),1.0]])]});
            var Q46;
            Q46=makeQuery(id+"F5.imprint","IMPRINT",FACE,{"disambiguationData":[TD([[makeQuery(id+"F5.imprint","IMPRINT",EDGE,{"derivedFrom":sQuery(id+"F5.wireOp",EDGE,"E20.6.0.0")}),1.0]])]});
            var Q47;
            Q47=makeQuery(id+"F5.imprint","IMPRINT",FACE,{"disambiguationData":[TD([[makeQuery(id+"F5.imprint","IMPRINT",EDGE,{"derivedFrom":sQuery(id+"F5.wireOp",EDGE,"E20.7.0.0")}),1.0]])]});
            var Q48;
            Q48=makeQuery(id+"F5.imprint","IMPRINT",FACE,{"disambiguationData":[TD([[makeQuery(id+"F5.imprint","IMPRINT",EDGE,{"derivedFrom":sQuery(id+"F5.wireOp",EDGE,"E20.8.0.0")}),1.0]])]});
            var Q49;
            Q49=makeQuery(id+"F5.imprint","IMPRINT",FACE,{"disambiguationData":[TD([[makeQuery(id+"F5.imprint","IMPRINT",EDGE,{"derivedFrom":sQuery(id+"F5.wireOp",EDGE,"E20.9.0.0")}),1.0]])]});
            extrude(context, id + "F6", {"entities" : qUnion([Q0, Q1, Q2, Q3, Q4, Q5, Q6, Q7, Q8, Q9, Q10, Q11, Q12, Q13, Q14, Q15, Q16, Q17, Q18, Q19, Q20, Q21, Q22, Q23, Q24, Q25, Q26, Q27, Q28, Q29, Q30, Q31, Q32, Q33, Q34, Q35, Q36, Q37, Q38, Q39, Q40, Q41, Q42, Q43, Q44, Q45, Q46, Q47, Q48, Q49]), "operationType" : NewBodyOperationType.REMOVE, "oppositeDirection" : true, "depth" : 15.24 * mm});
        }
        {
            var Q0;
            Q0=makeQuery(id+"F1.opExtrude","SWEPT_FACE",FACE,{"disambiguationData":[OSD([sQuery(id+"F0.wireOp",EDGE,"E0.top")])]});
            var sketch = newSketch(context, id + "F7", { "sketchPlane" : qUnion([Q0])});
            skText(sketch, "E21", { "text": "5.56x45 mm", "fontName": "OpenSans-Regular.ttf"});
            const initialGuessF7  = {"E21": [0.06907, 0.00793, 1, 0, 0.00318]};
            skSetInitialGuess(sketch, initialGuessF7);
            skSolve(sketch);
        }
        {
            var Q0;
            Q0 = qSketchRegion(id + "F7", true);
            extrude(context, id + "F8", {"entities" : qUnion([Q0]), "operationType" : NewBodyOperationType.REMOVE, "oppositeDirection" : true, "depth" : 1.59 * mm});
        }
    });
